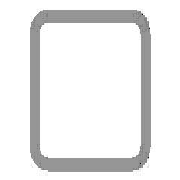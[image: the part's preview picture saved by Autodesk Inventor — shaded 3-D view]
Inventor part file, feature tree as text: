
AUTODESK INVENTOR PART (.ipt)
format: ipt  version: 2024 (Build 280153000, 153)  size: 137,216 bytes
history: native  units: mm (DEFAULTED — no unit token found)
features: other x4, plane x3, split x2, extrude x1, sketch x1
ambient origin geometry x8: Origin, YZ Plane, XZ Plane, XY Plane, X Axis, Y Axis, Z Axis, Center Point
bodies: Solid1 (feature_tree)
feature tree (11):
  parser-record x1  (decoder bookkeeping rows leaked as tree rows — omitted from the tree; the rows remain in map.json)
  other  "Driven Length"
  other  "Plano inicial"
  other  "Plano final"
  extrude  "Cuerpo"  TaperAngle=0.0deg  [1 undecoded]
  plane  "Plano de trabajo4"
  split  "Dividir1"
  plane  "Plano de trabajo5"
  split  "Dividir2"
  sketch  "Sketch3"  dims[d3=449.2mm d4=0.0mm d10=50.8mm d11=50.8mm d12=3.175mm d13=25.4mm d14=474.6mm d15=25.4mm d16=25.4mm d17=6.35mm d18=90.0deg d19=449.2mm]
  plane  "Work Plane3"
note: 1 required parameter value undecoded (feature->parameter linkage not recoverable at this tier; creation-order binding heuristic only, values carry confidence <= 0.55)
